# Revit family: Hager-FW-IP30-With_Door-With_notch-sistema-PT-pt
name_source: partatom
category: Electrical Equipment
units: mm (PartAtom-declared; Revit-internal decimal feet)

## family parameters
Cut with Voids When Loaded = No
Host = Face
Panel Configuration = Two Columns, Circuits Across
Part Type = Panelboard
Room Calculation Point = No
Round Connector Dimension = Use Diameter
Shared = No

## types (19) — shared parameters
EF000003 - Método de montagem = EV000128 - Parede oca
EF000007 - Cor = EV000202 - Branco
EF000049 - Profundidade = 125 mm  [stored 0.410105 ft]
EF000118 - Com tampa de montagem = No
EF000218 - Profundidade incorporada = 112 mm  [stored 0.367454 ft]
EF000339 - Tipo de difusor = EV004216 - Porta
EF001062 - Versão EMC = No
EF001088 - Extensão possível = Yes
EF001596 - Material do corpo = EV000179 - Aço
EF004462 - Tipo de fecho = EV000154 - Outro
EF005474 - Grau de proteção (IP) = EV006410 - IP30
EF006244 - Tampa/porta transparente = No
EF006306 - Com fecho = No
EF009212 - Tipo de tampa = EV009916 - Com recuo
EF015941 - Porta para passagem de sinal = No
HG000002 - Com porta ou tampa = Yes
HG000003 - Gama = FW
HG000005 - Espessura = 3 mm  [stored 0.00984252 ft]
HG000006 - Encastrado = Yes
HG000011 - Filas vazias desde da parte de baixo = No
HG000017 - Distância entre polos = 18 mm  [stored 0.0590551 ft]
Manufacturer = Hager
Type Comments = FW
zero-valued in all types: Default Elevation, HG000007 - Número de colunas vazias, HG000008 - Número de filas vazias

## per-type parameters (varying)
| type | EF000008 - Largura | EF000040 - Altura | EF000116 - Número RAL | EF000266 - Número de linhas | EF000332 - Altura embutida | EF000846 - Largura para embutir | EF001131 - Profundidade interior | EF001134 - Calha DIN | EF002950 - Largura em número de módulos | EF015776 - Borne de terra | EF015777 - Borne de neutro | HG000001 - Número de colunas | HG000004 - Referência do Fabricante | HG000009 - Porta dupla | HG000010 - Portas assimétricas | Model |
| Montagem embutida IP30 L353 A1003 P125 12 unidade de divisão - FWU61S | 353 mm  [stored 1.15814 ft] | 1003 mm  [stored 3.29068 ft] | 9010 | 6 | 952 mm  [stored 3.12336 ft] | 310 mm  [stored 1.01706 ft] | 112 mm  [stored 0.367454 ft] | Yes | 12 | Yes | No | 1 | FWU61S | No | No | FWU61S |
| Montagem embutida IP30 L353 A1153 P125 12 unidade de divisão - FWU71S | 353 mm  [stored 1.15814 ft] | 1153 mm | 9010 | 7 | 1102 mm  [stored 3.61549 ft] | 310 mm  [stored 1.01706 ft] | 112 mm  [stored 0.367454 ft] | Yes | 12 | Yes | No | 1 | FWU71S | No | No | FWU71S |
| Montagem embutida IP30 L353 A553 P125 12 unidade de divisão - FWU31S | 353 mm  [stored 1.15814 ft] | 553 mm  [stored 1.8143 ft] | 9010 | 3 | 502 mm  [stored 1.64698 ft] | 310 mm  [stored 1.01706 ft] | 112 mm  [stored 0.367454 ft] | Yes | 12 | Yes | Yes | 1 | FWU31S | No | No | FWU31S |
| Montagem embutida IP30 L353 A703 P125 12 unidade de divisão - FWU41S | 353 mm  [stored 1.15814 ft] | 703 mm  [stored 2.30643 ft] | 9010 | 4 | 652 mm  [stored 2.13911 ft] | 310 mm  [stored 1.01706 ft] | 112 mm  [stored 0.367454 ft] | Yes | 12 | Yes | No | 1 | FWU41S | No | No | FWU41S |
| Montagem embutida IP30 L353 A853 P125 12 unidade de divisão - FWU51S | 353 mm  [stored 1.15814 ft] | 853 mm  [stored 2.79856 ft] | 9010 | 5 | 802 mm  [stored 2.63123 ft] | 310 mm  [stored 1.01706 ft] | 112 mm  [stored 0.367454 ft] | Yes | 12 | Yes | No | 1 | FWU51S | No | No | FWU51S |
| Montagem embutida IP30 L603 A1003 P125 12 unidade de divisão - FWU62S | 603 mm | 1003 mm  [stored 3.29068 ft] | 9010 | 12 | 952 mm  [stored 3.12336 ft] | 560 mm  [stored 1.83727 ft] | 112 mm  [stored 0.367454 ft] | Yes | 12 | Yes | No | 2 | FWU62S | No | No | FWU62S |
| Montagem embutida IP30 L603 A1003 P125 26 unidade de divisão - FWU62M2 | 603 mm | 1003 mm  [stored 3.29068 ft] | 9010 | 6 | 952 mm  [stored 3.12336 ft] | 560 mm  [stored 1.83727 ft] | 112 mm  [stored 0.367454 ft] | Yes | 26 | No | No | 1 | FWU62M2 | No | No | FWU62M2 |
| Montagem embutida IP30 L603 A1153 P125 12 unidade de divisão - FWU72S | 603 mm | 1153 mm | 9010 | 14 | 1102 mm  [stored 3.61549 ft] | 560 mm  [stored 1.83727 ft] | 112 mm  [stored 0.367454 ft] | Yes | 12 | Yes | No | 2 | FWU72S | No | No | FWU72S |
| Montagem embutida IP30 L603 A1153 P125 26 unidade de divisão - FWU72M2 | 603 mm | 1153 mm | 9010 | 7 | 1102 mm  [stored 3.61549 ft] | 560 mm  [stored 1.83727 ft] | 112 mm  [stored 0.367454 ft] | Yes | 26 | No | No | 1 | FWU72M2 | No | No | FWU72M2 |
| Montagem embutida IP30 L603 A553 P125 12 unidade de divisão - FWU32S | 603 mm | 553 mm  [stored 1.8143 ft] | 9010 | 6 | 502 mm  [stored 1.64698 ft] | 560 mm  [stored 1.83727 ft] | 112 mm  [stored 0.367454 ft] | Yes | 12 | Yes | No | 2 | FWU32S | No | No | FWU32S |
| Montagem embutida IP30 L603 A553 P125 26 unidade de divisão - FWU32M2 | 603 mm | 553 mm  [stored 1.8143 ft] | 9010 | 3 | 502 mm  [stored 1.64698 ft] | 560 mm  [stored 1.83727 ft] | 112 mm  [stored 0.367454 ft] | Yes | 26 | No | No | 1 | FWU32M2 | No | No | FWU32M2 |
| Montagem embutida IP30 L603 A703 P125 12 unidade de divisão - FWU42S | 603 mm | 703 mm  [stored 2.30643 ft] | 9010 | 8 | 652 mm  [stored 2.13911 ft] | 560 mm  [stored 1.83727 ft] | 112 mm  [stored 0.367454 ft] | Yes | 12 | Yes | No | 2 | FWU42S | No | No | FWU42S |
| Montagem embutida IP30 L603 A703 P125 26 unidade de divisão - FWU42M2 | 603 mm | 703 mm  [stored 2.30643 ft] | 9010 | 4 | 652 mm  [stored 2.13911 ft] | 560 mm  [stored 1.83727 ft] | 110 mm  [stored 0.360892 ft] | Yes | 26 | No | No | 1 | FWU42M2 | No | No | FWU42M2 |
| Montagem embutida IP30 L603 A853 P125 12 unidade de divisão - FWU52S | 603 mm | 853 mm  [stored 2.79856 ft] | 9010 | 10 | 802 mm  [stored 2.63123 ft] | 560 mm  [stored 1.83727 ft] | 112 mm  [stored 0.367454 ft] | Yes | 12 | Yes | No | 2 | FWU52S | No | No | FWU52S |
| Montagem embutida IP30 L603 A853 P125 26 unidade de divisão - FWU52M2 | 603 mm | 853 mm  [stored 2.79856 ft] | 9010 | 5 | 802 mm  [stored 2.63123 ft] | 560 mm  [stored 1.83727 ft] | 110 mm  [stored 0.360892 ft] | Yes | 26 | No | No | 1 | FWU52M2 | No | No | FWU52M2 |
| Montagem embutida IP30 L853 A1003 P125 12 unidade de divisão - FWU63S | 853 mm  [stored 2.79856 ft] | 1003 mm  [stored 3.29068 ft] | 9010 | 18 | 952 mm  [stored 3.12336 ft] | 810 mm | 112 mm  [stored 0.367454 ft] | Yes | 12 | Yes | No | 3 | FWU63S | Yes | Yes | FWU63S |
| Montagem embutida IP30 L853 A1153 P125 12 unidade de divisão - FWU73S | 853 mm  [stored 2.79856 ft] | 1153 mm | 9010 | 21 | 1102 mm  [stored 3.61549 ft] | 810 mm | 112 mm  [stored 0.367454 ft] | Yes | 12 | Yes | Yes | 3 | FWU73S | Yes | Yes | FWU73S |
| Montagem embutida IP30 L853 A703 P125 12 unidade de divisão - FWU43S | 853 mm  [stored 2.79856 ft] | 703 mm  [stored 2.30643 ft] | 9010 | 12 | 652 mm  [stored 2.13911 ft] | 810 mm | 112 mm  [stored 0.367454 ft] | Yes | 12 | Yes | No | 3 | FWU43S | Yes | Yes | FWU43S |
| Montagem embutida IP30 L853 A853 P125 12 unidade de divisão - FWU53S | 853 mm  [stored 2.79856 ft] | 853 mm  [stored 2.79856 ft] |  | 15 | 802 mm  [stored 2.63123 ft] | 810 mm | 112 mm  [stored 0.367454 ft] | No | 12 | Yes | No | 3 | FWU53S | Yes | Yes | FWU53S |

note: [stored X ft] marks values corroborated as IEEE doubles in the binary element streams (Revit-internal decimal feet)

## geometry (parser evidence)
native form markers: Sweep x17
no freeform markers — native parametric forms only
